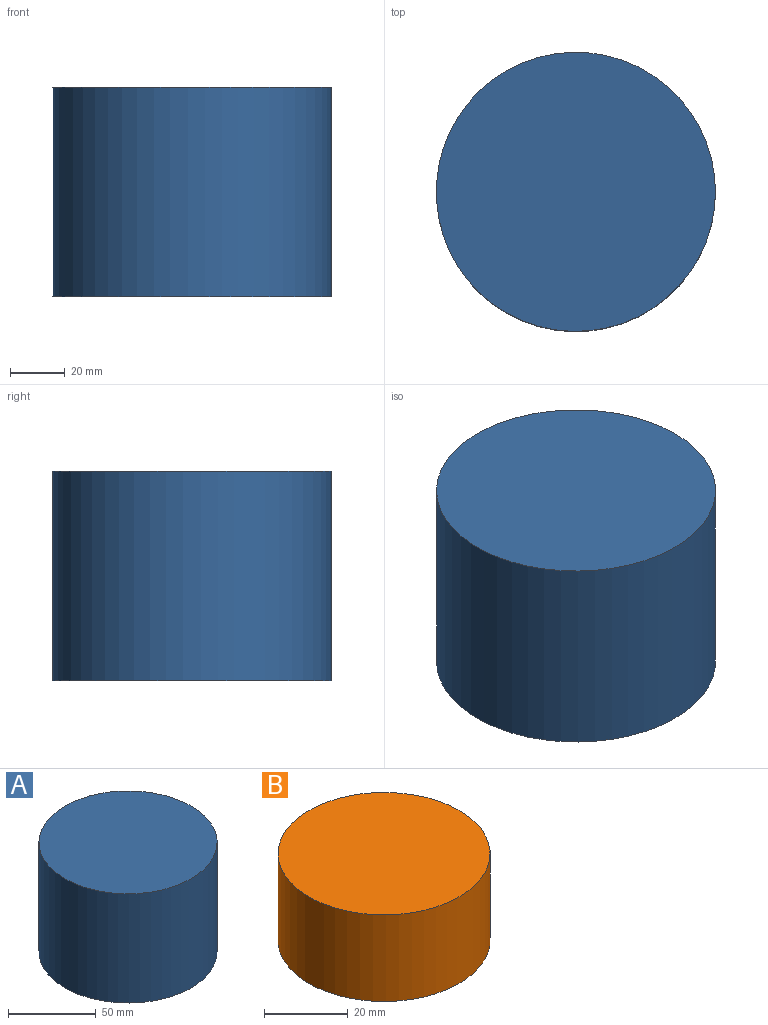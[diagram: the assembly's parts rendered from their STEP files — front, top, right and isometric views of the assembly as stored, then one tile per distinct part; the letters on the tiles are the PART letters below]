
ASSEMBLY  parts=2 mates=1
PART A: 5 faces, bbox 101.6x101.6x76.2 mm
  f0: cylinder r=50.8mm len=101.6mm, axis (0,0,-1), area 24322mm2, adj f1,f2
  f1: plane 101.6x101.6mm, normal (0,0,1), area 8107.3mm2, adj f0
  f2: plane 101.6x101.6mm, normal (0,0,-1), area 981.7mm2, adj f0,f3
  f3: cylinder r=47.62mm len=95.25mm, axis (0,0,-1), area 20901.7mm2, adj f2,f4
  f4: plane 95.25x95.25mm, normal (0,0,-1), area 7125.6mm2, adj f3
PART B: 5 faces, bbox 50.8x50.8x25.4 mm
  f0: cylinder r=25.4mm len=50.8mm, axis (0,0,-1), area 4053.7mm2, adj f1,f2
  f1: plane 50.8x50.8mm, normal (0,0,1), area 2026.8mm2, adj f0
  f2: plane 50.8x50.8mm, normal (0,0,-1), area 475mm2, adj f0,f3
  f3: cylinder r=22.23mm len=44.45mm, axis (0,0,-1), area 2660.2mm2, adj f2,f4
  f4: plane 44.45x44.45mm, normal (0,0,-1), area 1551.8mm2, adj f3
PLACE A t=(20.65,-71.61,6.01)mm
PLACE B t=(-0.19,-52.25,50.46)mm
MATE slider B.f0 <-> A.f0  axis (0,0,-1) through (-26.37,-32.9,75.86)mm
